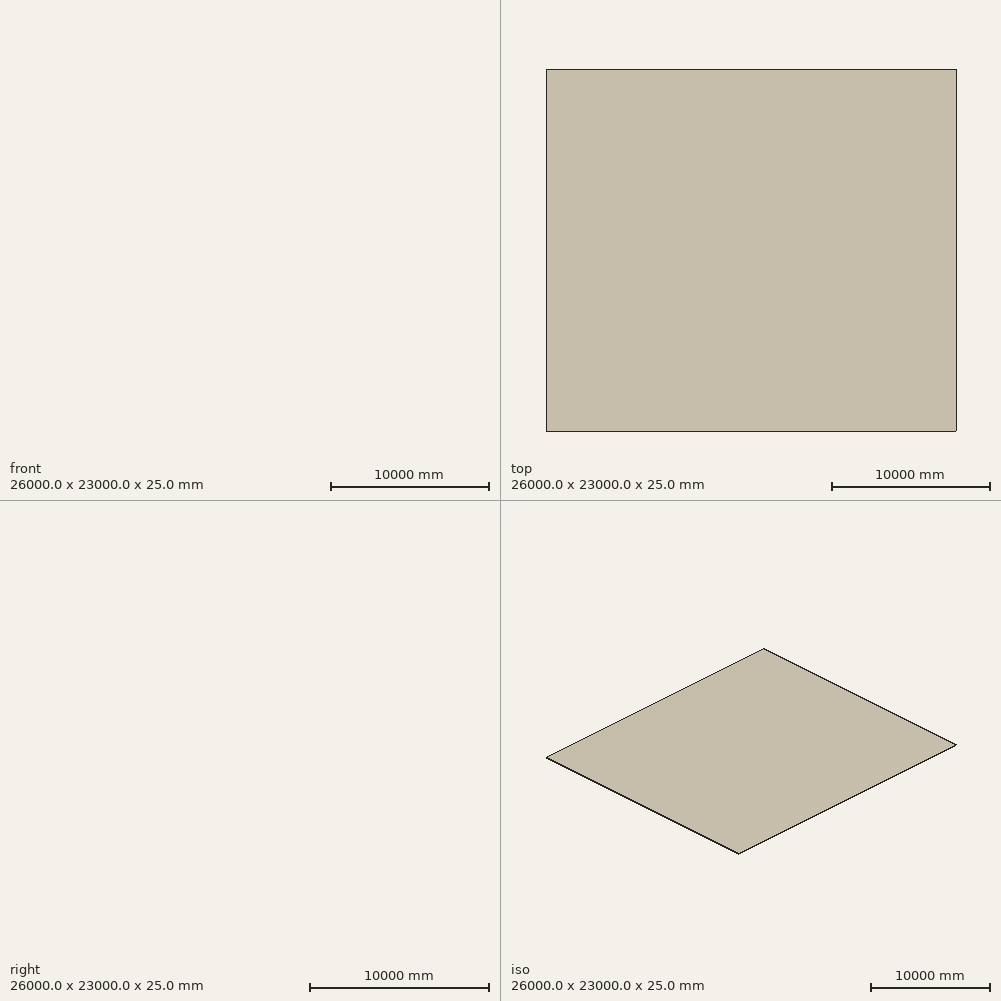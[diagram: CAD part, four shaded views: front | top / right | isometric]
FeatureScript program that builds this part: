
annotation { "Feature Type Name" : "Feature", "Feature Type Description" : "" }
export const myFeature = defineFeature(function(context is Context, id is Id, definition is map)
    precondition{}
    {
        {
            var Q0;
            Q0=qCreatedBy(makeId("Top.planeOp"),FACE);
            var sketch = newSketch(context, id + "F0", { "sketchPlane" : qUnion([Q0])});
            skLineSegment(sketch, "E0.bottom", {"start": v(0, 0) * mm, "end": v(-26000, 0) * mm});
            skLineSegment(sketch, "E0.top", {"start": v(0, 23000) * mm, "end": v(-26000, 23000) * mm});
            skLineSegment(sketch, "E0.left", {"start": v(0, 0) * mm, "end": v(0, 23000) * mm});
            skLineSegment(sketch, "E0.right", {"start": v(-26000, 0) * mm, "end": v(-26000, 23000) * mm});
            skSolve(sketch);
        }
        {
            var Q0;
            Q0=makeQuery(id+"F0.imprint","IMPRINT",FACE,{"disambiguationData":[TD([[makeQuery(id+"F0.imprint","IMPRINT",EDGE,{"derivedFrom":sQuery(id+"F0.wireOp",EDGE,"E0.bottom")}),-1.0]])]});
            var Q1;
            Q1 = qSketchRegion(id + "F2", true);
            extrude(context, id + "F1", {"entities" : qUnion([Q0, Q1]), "depth" : 25 * mm, "offsetDistance" : 25 * mm});
        }
        {
            var Q0;
            Q0=makeQuery(id+"F1.opExtrude","CAP_FACE",FACE,{"disambiguationData":[OSD([sQuery(id+"F0.wireOp",EDGE,"E0.bottom"),sQuery(id+"F0.wireOp",EDGE,"E0.top"),sQuery(id+"F0.wireOp",EDGE,"E0.left"),sQuery(id+"F0.wireOp",EDGE,"E0.right")])],"isStart":false});
            var sketch = newSketch(context, id + "F2", { "sketchPlane" : qUnion([Q0])});
            skLineSegment(sketch, "E1.bottom", {"start": v(-26000, 23000) * mm, "end": v(-9000, 23000) * mm});
            skLineSegment(sketch, "E1.top", {"start": v(-26000, 5000) * mm, "end": v(-9000, 5000) * mm});
            skLineSegment(sketch, "E1.left", {"start": v(-26000, 23000) * mm, "end": v(-26000, 5000) * mm});
            skLineSegment(sketch, "E1.right", {"start": v(-9000, 23000) * mm, "end": v(-9000, 5000) * mm});
            skLineSegment(sketch, "E2", {"start": v(-9000, 23000) * mm, "end": v(-6000, 23000) * mm});
            skLineSegment(sketch, "E3", {"start": v(-6000, 23000) * mm, "end": v(-6000, 0) * mm});
            skLineSegment(sketch, "E4", {"start": v(-26000, 5000) * mm, "end": v(-26000, 0) * mm});
            skLineSegment(sketch, "E5", {"start": v(-6000, 23000) * mm, "end": v(0, 23000) * mm});
            skLineSegment(sketch, "E6", {"start": v(0, 23000) * mm, "end": v(0, 0) * mm});
            skLineSegment(sketch, "E7", {"start": v(-6000, 23000) * mm, "end": v(-6000, 19000) * mm});
            skLineSegment(sketch, "E8", {"start": v(-6000, 19000) * mm, "end": v(-6000, 14000) * mm});
            skLineSegment(sketch, "E9", {"start": v(-6000, 0) * mm, "end": v(-6000, 5000) * mm});
            skLineSegment(sketch, "E10", {"start": v(-6000, 14000) * mm, "end": v(-6000, 5000) * mm});
            skLineSegment(sketch, "E11", {"start": v(-26000, 0) * mm, "end": v(-26000, 2000) * mm});
            skLineSegment(sketch, "E12", {"start": v(-26000, 2000) * mm, "end": v(-9000, 2000) * mm});
            skLineSegment(sketch, "E13", {"start": v(-9000, 2000) * mm, "end": v(-9000, 0) * mm});
            skSolve(sketch);
        }
    });
